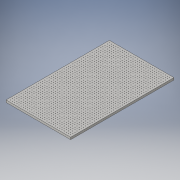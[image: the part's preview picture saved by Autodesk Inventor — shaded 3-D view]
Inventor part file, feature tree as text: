
AUTODESK INVENTOR PART (.ipt)
format: ipt  version: 2016 (Build 200138000, 138)  size: 1,199,616 bytes
history: native  units: in
note: dims shown in document units (in); Inventor stores cm internally (conversion verified against a paired STEP export)
features: sketch x2, extrude x1, hole x1, pattern_linear x1
ambient origin geometry x8: Origin, YZ Plane, XZ Plane, XY Plane, X Axis, Y Axis, Z Axis, Center Point
bodies: Solid1 (feature_tree)
feature tree (5):
  extrude  "Extrusion1"  Depth=30.0in
  hole  "Hole1"  [1 undecoded]
  pattern_linear  "Rectangular Pattern1"  Spacing1=1.0in  [1 undecoded]
  sketch  "Sketch1"  dims[d0=48.0in d1=30.0in]
  sketch  "Sketch2"  dims[d2=1.0in d3=0.0in d4=1.0in d5=1.0in d6=0.196in d7=0.5in d8=0.375in d9=0.25in d10=0.5635in d11=1.0in d12=0.8108in d13=11.4173in d15=1.0in d16=18.5039in d18=1.0in]
note: 2 required parameter values undecoded (feature->parameter linkage not recoverable at this tier; creation-order binding heuristic only, values carry confidence <= 0.55)
